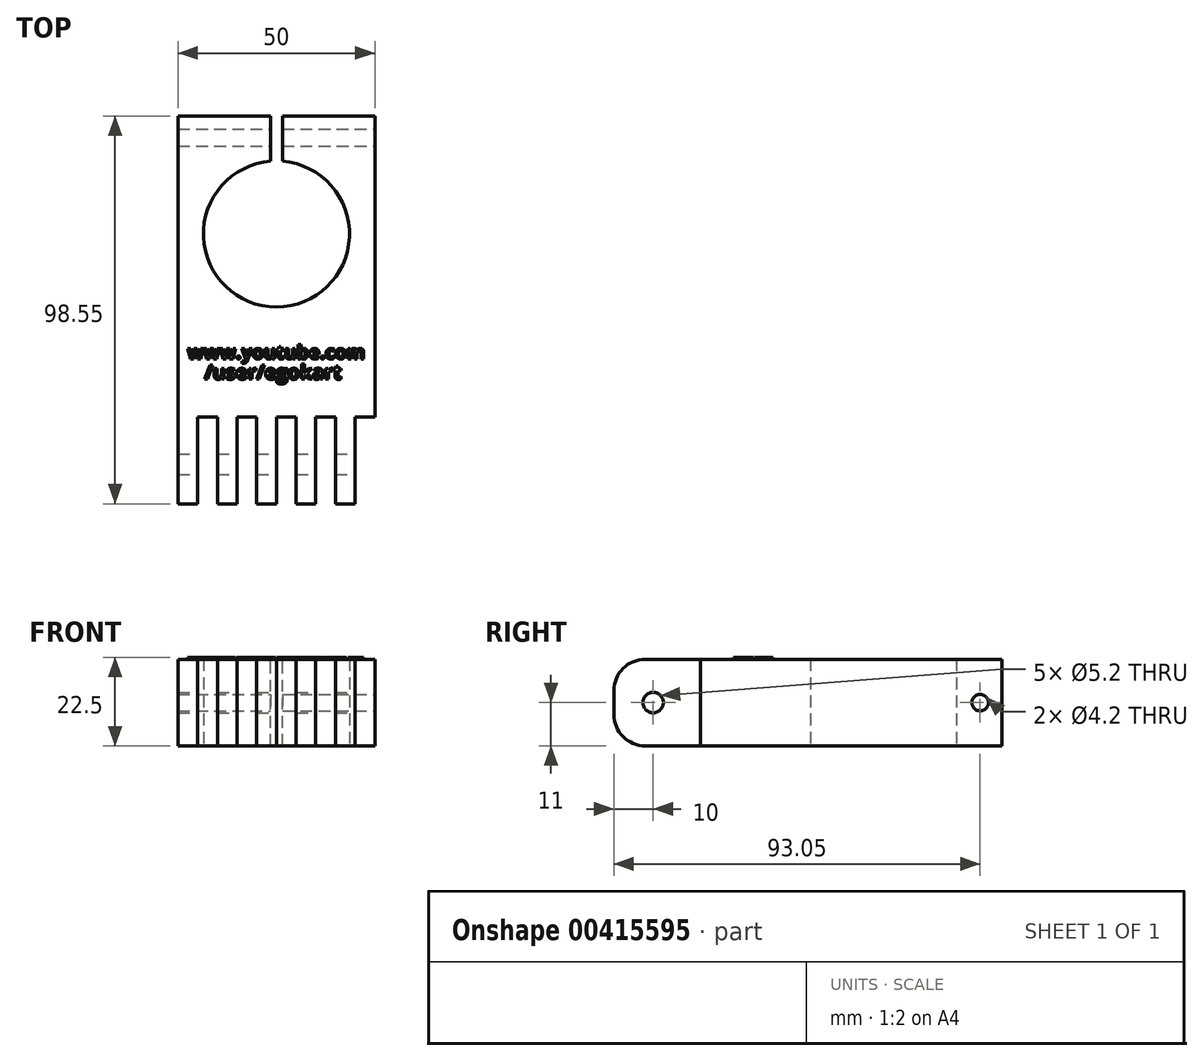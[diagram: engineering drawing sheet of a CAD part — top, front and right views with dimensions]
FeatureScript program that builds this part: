
annotation { "Feature Type Name" : "Feature", "Feature Type Description" : "" }
export const myFeature = defineFeature(function(context is Context, id is Id, definition is map)
    precondition{}
    {
        {
            var Q0;
            Q0=qCreatedBy(makeId("Top.planeOp"),FACE);
            var sketch = newSketch(context, id + "F0", { "sketchPlane" : qUnion([Q0])});
            skPoint(sketch, "E0.middle", {"position": v(0, 0) * mm});
            skCircle(sketch, "E1", {"center": v(0, 0) * mm, "radius": 18.55 * mm});
            skLineSegment(sketch, "E2.bottom", {"start": v(-25, -68.55) * mm, "end": v(25, -68.55) * mm});
            skLineSegment(sketch, "E2.top", {"start": v(-25, 30) * mm, "end": v(25, 30) * mm});
            skLineSegment(sketch, "E2.left", {"start": v(-25, -68.55) * mm, "end": v(-25, 30) * mm});
            skLineSegment(sketch, "E2.right", {"start": v(25, -68.55) * mm, "end": v(25, 30) * mm});
            skSolve(sketch);
        }
        {
            var Q0;
            Q0=makeQuery(id+"F0.imprint","IMPRINT",FACE,{"disambiguationData":[TD([[makeQuery(id+"F0.imprint","IMPRINT",EDGE,{"derivedFrom":sQuery(id+"F0.wireOp",EDGE,"E1")}),-1.0]])]});
            extrude(context, id + "F1", {"entities" : qUnion([Q0]), "depth" : 22 * mm});
        }
        {
            var Q0;
            Q0=makeQuery(id+"F1.opExtrude","SWEPT_FACE",FACE,{"disambiguationData":[OSD([sQuery(id+"F0.wireOp",EDGE,"E2.bottom")])]});
            var sketch = newSketch(context, id + "F2", { "sketchPlane" : qUnion([Q0])});
            skLineSegment(sketch, "E3", {"start": v(-20, 22) * mm, "end": v(-20, 0) * mm});
            skLineSegment(sketch, "E4.0", {"start": v(-15, 22) * mm, "end": v(-15, 0) * mm});
            skLineSegment(sketch, "E5.0", {"start": v(-10, 22) * mm, "end": v(-10, 0) * mm});
            skLineSegment(sketch, "E6.0", {"start": v(-5, 22) * mm, "end": v(-5, 0) * mm});
            skLineSegment(sketch, "E7.0", {"start": v(0, 22) * mm, "end": v(0, 0) * mm});
            skLineSegment(sketch, "E8.0", {"start": v(5, 22) * mm, "end": v(5, 0) * mm});
            skLineSegment(sketch, "E9.0", {"start": v(10, 22) * mm, "end": v(10, 0) * mm});
            skLineSegment(sketch, "E10.0", {"start": v(15, 22) * mm, "end": v(15, 0) * mm});
            skLineSegment(sketch, "E11.0", {"start": v(20, 22) * mm, "end": v(20, 0) * mm});
            skSolve(sketch);
        }
        {
            var Q0;
            Q0=makeQuery(id+"F1.opExtrude","CAP_EDGE",EDGE,{"disambiguationData":[OSD([sQuery(id+"F0.wireOp",EDGE,"E2.bottom")])],"isStart":false});
            var Q1;
            Q1=makeQuery(id+"F1.opExtrude","CAP_EDGE",EDGE,{"disambiguationData":[OSD([sQuery(id+"F0.wireOp",EDGE,"E2.bottom")])],"isStart":true});
            fillet(context, id + "F3", {"entities" : qUnion([Q0, Q1]), "radius" : 8 * mm, "tangentPropagation" : true, "allowEdgeOverflow" : false});
        }
        {
            var Q0;
            {var subQ0=sQuery(id+"F2.wireOp",EDGE,"E3");Q0=makeQuery(id+"F2.imprint","IMPRINT",FACE,{"disambiguationData":[TD([[makeQuery(id+"F2.imprint","IMPRINT",EDGE,{"derivedFrom":subQ0}),1.0]])]});}
            var Q1;
            {var subQ0=sQuery(id+"F2.wireOp",EDGE,"E5.0");Q1=makeQuery(id+"F2.imprint","IMPRINT",FACE,{"disambiguationData":[TD([[makeQuery(id+"F2.imprint","IMPRINT",EDGE,{"derivedFrom":subQ0}),1.0]])]});}
            var Q2;
            {var subQ0=sQuery(id+"F2.wireOp",EDGE,"E7.0");Q2=makeQuery(id+"F2.imprint","IMPRINT",FACE,{"disambiguationData":[TD([[makeQuery(id+"F2.imprint","IMPRINT",EDGE,{"derivedFrom":subQ0}),1.0]])]});}
            var Q3;
            {var subQ0=sQuery(id+"F2.wireOp",EDGE,"E9.0");Q3=makeQuery(id+"F2.imprint","IMPRINT",FACE,{"disambiguationData":[TD([[makeQuery(id+"F2.imprint","IMPRINT",EDGE,{"derivedFrom":subQ0}),1.0]])]});}
            var Q4;
            {var subQ0=sQuery(id+"F2.wireOp",EDGE,"E11.0");Q4=makeQuery(id+"F2.imprint","IMPRINT",FACE,{"disambiguationData":[TD([[makeQuery(id+"F2.imprint","IMPRINT",EDGE,{"derivedFrom":subQ0}),1.0]])]});}
            extrude(context, id + "F4", {"entities" : qUnion([Q0, Q1, Q2, Q3, Q4]), "operationType" : NewBodyOperationType.REMOVE, "oppositeDirection" : true, "depth" : 22 * mm});
        }
        {
            var Q0;
            Q0=makeQuery(id+"F1.opExtrude","SWEPT_FACE",FACE,{"disambiguationData":[OSD([sQuery(id+"F0.wireOp",EDGE,"E2.top")])]});
            var sketch = newSketch(context, id + "F5", { "sketchPlane" : qUnion([Q0])});
            skLineSegment(sketch, "E12.bottom", {"start": v(1.5, 0) * mm, "end": v(-1.5, 0) * mm});
            skLineSegment(sketch, "E12.top", {"start": v(1.5, 22) * mm, "end": v(-1.5, 22) * mm});
            skLineSegment(sketch, "E12.left", {"start": v(1.5, 0) * mm, "end": v(1.5, 22) * mm});
            skLineSegment(sketch, "E12.right", {"start": v(-1.5, 0) * mm, "end": v(-1.5, 22) * mm});
            skPoint(sketch, "E12.middle", {"position": v(0, 11) * mm});
            skPoint(sketch, "E12.middle.positionSnap0", {"position": v(-25, 11) * mm});
            skPoint(sketch, "E12.centerSnap0", {"position": v(-25, 11) * mm});
            skSolve(sketch);
        }
        {
            var Q0;
            Q0=makeQuery(id+"F5.imprint","IMPRINT",FACE,{"disambiguationData":[TD([[makeQuery(id+"F5.imprint","IMPRINT",EDGE,{"derivedFrom":sQuery(id+"F5.wireOp",EDGE,"E12.bottom")}),-1.0]])]});
            extrude(context, id + "F6", {"entities" : qUnion([Q0]), "operationType" : NewBodyOperationType.REMOVE, "oppositeDirection" : true, "depth" : 18 * mm});
        }
        {
            var Q0;
            Q0=makeQuery(id+"F1.opExtrude","SWEPT_FACE",FACE,{"disambiguationData":[OSD([sQuery(id+"F0.wireOp",EDGE,"E2.right")])]});
            var sketch = newSketch(context, id + "F7", { "sketchPlane" : qUnion([Q0])});
            skCircle(sketch, "E13", {"center": v(24.5, 11) * mm, "radius": 2.1 * mm});
            skPoint(sketch, "E13.centerSnap0", {"position": v(30, 11) * mm});
            skCircle(sketch, "E14", {"center": v(-58.55, 11) * mm, "radius": 2.6 * mm});
            skSolve(sketch);
        }
        {
            var Q0;
            Q0=makeQuery(id+"F7.imprint","IMPRINT",FACE,{"disambiguationData":[TD([[makeQuery(id+"F7.imprint","IMPRINT",EDGE,{"derivedFrom":sQuery(id+"F7.wireOp",EDGE,"E13")}),1.0]])]});
            var Q1;
            Q1=makeQuery(id+"F7.imprint","IMPRINT",FACE,{"disambiguationData":[TD([[makeQuery(id+"F7.imprint","IMPRINT",EDGE,{"derivedFrom":sQuery(id+"F7.wireOp",EDGE,"E14")}),1.0]])]});
            extrude(context, id + "F8", {"entities" : qUnion([Q0, Q1]), "operationType" : NewBodyOperationType.REMOVE, "endBound" : BoundingType.THROUGH_ALL, "oppositeDirection" : true, "depth" : 25 * mm});
        }
        {
            var Q0;
            Q0=makeQuery(id+"F1.opExtrude","CAP_FACE",FACE,{"disambiguationData":[OSD([sQuery(id+"F0.wireOp",EDGE,"E1"),sQuery(id+"F0.wireOp",EDGE,"E2.bottom"),sQuery(id+"F0.wireOp",EDGE,"E2.top"),sQuery(id+"F0.wireOp",EDGE,"E2.left"),sQuery(id+"F0.wireOp",EDGE,"E2.right")])],"isStart":false});
            var sketch = newSketch(context, id + "F9", { "sketchPlane" : qUnion([Q0])});
            skPoint(sketch, "E15.secondSnap0", {"position": v(22.5, -46.55) * mm});
            skText(sketch, "E16", { "text": "www.youtube.com", "fontName": "OpenSans-Bold.ttf"});
            skText(sketch, "E17", { "text": "/user/egokart", "fontName": "OpenSans-Bold.ttf"});
            const initialGuessF9  = {"E16": [-0.02258, -0.03173, 1, 0, 0.00345], "E17": [-0.01825, -0.0369, 1, 0, 0.00363]};
            skSetInitialGuess(sketch, initialGuessF9);
            skSolve(sketch);
        }
        {
            var Q0;
            Q0 = qSketchRegion(id + "F9", true);
            extrude(context, id + "F10", {"entities" : qUnion([Q0]), "operationType" : NewBodyOperationType.ADD, "depth" : 0.5 * mm});
        }
    });
